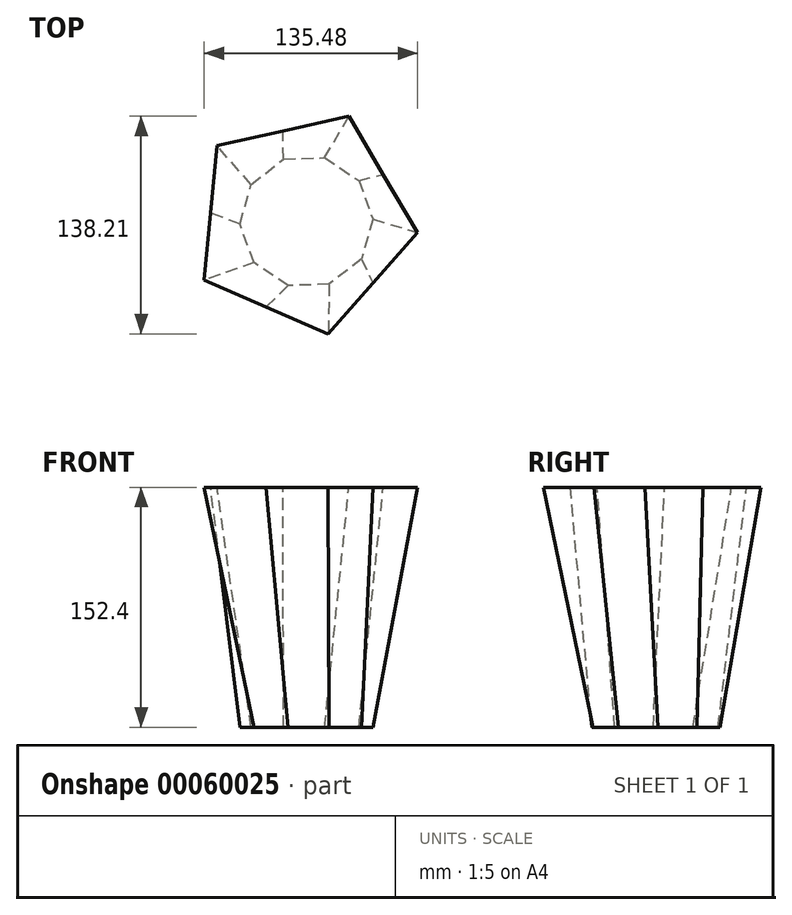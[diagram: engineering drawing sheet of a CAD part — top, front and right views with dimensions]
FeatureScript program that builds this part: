
annotation { "Feature Type Name" : "Feature", "Feature Type Description" : "" }
export const myFeature = defineFeature(function(context is Context, id is Id, definition is map)
    precondition{}
    {
        {
            var Q0;
            Q0=qCreatedBy(makeId("Top.planeOp"),FACE);
            var sketch = newSketch(context, id + "F0", { "sketchPlane" : qUnion([Q0])});
            skCircle(sketch, "E0.cCircle", {"center": v(2.03, 0) * mm, "radius": 40.2 * mm, "construction": true});
            skLineSegment(sketch, "E0.0", {"start": v(-31.24, -26.06) * mm, "end": v(-40.2, -1.53) * mm});
            skLineSegment(sketch, "E0.1", {"start": v(-40.2, -1.53) * mm, "end": v(-33.04, 23.6) * mm});
            skLineSegment(sketch, "E0.2", {"start": v(-33.04, 23.6) * mm, "end": v(-12.47, 39.7) * mm});
            skLineSegment(sketch, "E0.3", {"start": v(-12.47, 39.7) * mm, "end": v(13.63, 40.64) * mm});
            skLineSegment(sketch, "E0.4", {"start": v(13.63, 40.64) * mm, "end": v(35.3, 26.06) * mm});
            skLineSegment(sketch, "E0.5", {"start": v(35.3, 26.06) * mm, "end": v(44.27, 1.53) * mm});
            skLineSegment(sketch, "E0.6", {"start": v(44.27, 1.53) * mm, "end": v(37.1, -23.6) * mm});
            skLineSegment(sketch, "E0.7", {"start": v(37.1, -23.6) * mm, "end": v(16.54, -39.7) * mm});
            skLineSegment(sketch, "E0.8", {"start": v(16.54, -39.7) * mm, "end": v(-9.57, -40.64) * mm});
            skLineSegment(sketch, "E0.9", {"start": v(-9.57, -40.64) * mm, "end": v(-31.24, -26.06) * mm});
            skPoint(sketch, "E0.0.midPoint", {"position": v(-35.72, -13.8) * mm});
            skSolve(sketch);
        }
        {
            var Q0;
            Q0=qCreatedBy(makeId("Top.planeOp"),FACE);
            cPlane(context, id + "F1", {"entities" : qUnion([Q0]), "cplaneType" : CPlaneType.OFFSET, "offset" : 152.4 * mm, "width" : 152.4 * mm, "height" : 152.4 * mm});
        }
        {
            var Q0;
            Q0=qCreatedBy(id+"F1.planeOp",FACE);
            var sketch = newSketch(context, id + "F2", { "sketchPlane" : qUnion([Q0])});
            skCircle(sketch, "E1.cCircle", {"center": v(0, 0) * mm, "radius": 59.05 * mm, "construction": true});
            skLineSegment(sketch, "E1.0", {"start": v(28.98, 66.98) * mm, "end": v(72.66, -6.87) * mm});
            skLineSegment(sketch, "E1.1", {"start": v(72.66, -6.87) * mm, "end": v(15.92, -71.23) * mm});
            skLineSegment(sketch, "E1.2", {"start": v(15.92, -71.23) * mm, "end": v(-62.82, -37.15) * mm});
            skLineSegment(sketch, "E1.3", {"start": v(-62.82, -37.15) * mm, "end": v(-54.75, 48.26) * mm});
            skLineSegment(sketch, "E1.4", {"start": v(-54.75, 48.26) * mm, "end": v(28.98, 66.98) * mm});
            skPoint(sketch, "E1.0.midPoint", {"position": v(50.82, 30.06) * mm});
            skSolve(sketch);
        }
        {
            var Q0;
            Q0=makeQuery(id+"F0.imprint","IMPRINT",FACE,{"disambiguationData":[TD([[makeQuery(id+"F0.imprint","IMPRINT",EDGE,{"derivedFrom":sQuery(id+"F0.wireOp",EDGE,"E0.0")}),-1.0]])]});
            var Q1;
            Q1=makeQuery(id+"F2.imprint","IMPRINT",FACE,{"disambiguationData":[TD([[makeQuery(id+"F2.imprint","IMPRINT",EDGE,{"derivedFrom":sQuery(id+"F2.wireOp",EDGE,"E1.0")}),-1.0]])]});
            loft(context, id + "F3", {"sheetProfilesArray" : [{ "sheetProfileEntities" : qUnion([Q0]) }, { "sheetProfileEntities" : qUnion([Q1]) }]});
        }
    });
